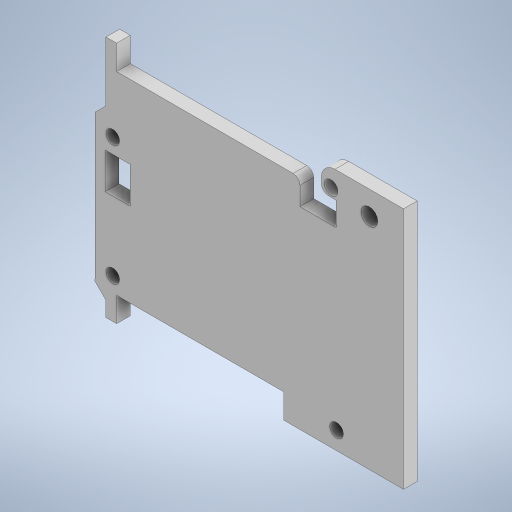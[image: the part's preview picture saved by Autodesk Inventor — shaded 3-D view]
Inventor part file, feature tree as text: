
AUTODESK INVENTOR PART (.ipt)
format: ipt  version: 2024 (Build 280153000, 153)  size: 711,680 bytes
history: native  units: in
note: dims shown in document units (in); Inventor stores cm internally (conversion verified against a paired STEP export)
features: extrude x7, sketch x6, projected_geometry x4, fillet x2
ambient origin geometry x8: Origin, YZ Plane, XZ Plane, XY Plane, X Axis, Y Axis, Z Axis, Center Point
bodies: Solid1 (feature_tree)
feature tree (19):
  extrude  "Extrusion1"  Depth=0.125in
  extrude  "Extrusion2"  Depth=0.015in
  extrude  "Extrusion3"  Depth=0.015in
  extrude  "Extrusion4"  Depth=0.005in
  extrude  "Extrusion5"  Depth=0.125in
  fillet  "Fillet1"  Radius=0.125in
  extrude  "Extrusion6"  Depth=0.125in
  extrude  "Extrusion7"  Depth=0.125in TaperAngle=0.0deg
  fillet  "Fillet2"  Radius=0.125in
  sketch  "Sketch3"  dims[d0=0.125in d1=0.0in d2=0.015in]
  projected_geometry  "Projected Loop1"
  sketch  "Sketch4"  dims[d3=0.015in d4=0.015in]
  projected_geometry  "Projected Loop2"
  sketch  "Sketch6"  dims[d5=0.015in d6=0.015in]
  projected_geometry  "Projected Loop3"
  sketch  "Sketch7"  dims[d7=0.015in d8=0.005in]
  projected_geometry  "Projected Loop4"
  sketch  "Sketch8"  dims[d9=1.0in d10=0.0in d11=0.125in d12=0.125in]
  sketch  "Sketch9"  dims[d13=0.125in d14=0.125in d15=0.125in d16=0.0in d17=0.125in d18=0.0in d19=0.125in d20=0.0in d21=0.063in d22=1.0in d23=0.0in d24=1.0in d25=0.0in d26=0.125in]
